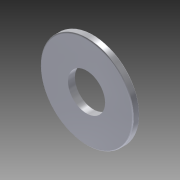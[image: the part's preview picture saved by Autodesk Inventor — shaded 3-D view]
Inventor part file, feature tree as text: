
AUTODESK INVENTOR PART (.ipt)
format: ipt  version: 2015 (Build 190159000, 159)  size: 114,688 bytes
history: native  units: mm
features: extrude x1, fillet x1, sketch x1
ambient origin geometry x8: Origin, YZ Plane, XZ Plane, XY Plane, X Axis, Y Axis, Z Axis, Center Point
bodies: Solid1 (feature_tree)
feature tree (3):
  extrude  "Extrusion1"  Depth=0.25mm
  fillet  "Fillet1"  Radius=1.5mm
  sketch  "Sketch1"  dims[d0=20.0mm d1=8.0mm d2=1.5mm d3=0.0mm d4=0.25mm]
